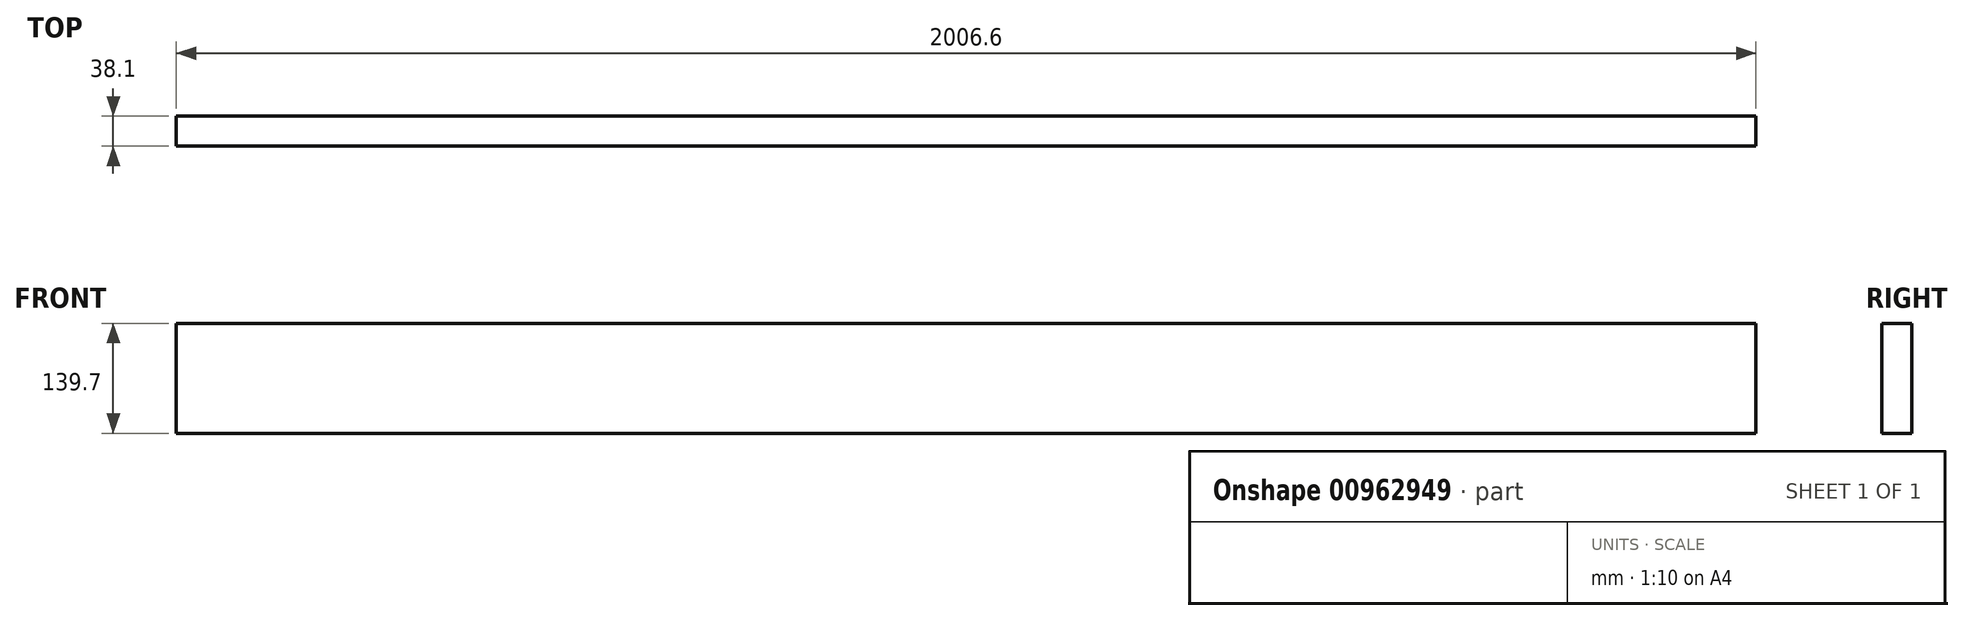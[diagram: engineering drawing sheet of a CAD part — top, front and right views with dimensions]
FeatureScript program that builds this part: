
annotation { "Feature Type Name" : "Feature", "Feature Type Description" : "" }
export const myFeature = defineFeature(function(context is Context, id is Id, definition is map)
    precondition{}
    {
        {
            var Q0;
            Q0=qCreatedBy(makeId("Right.planeOp"),FACE);
            var sketch = newSketch(context, id + "F0", { "sketchPlane" : qUnion([Q0])});
            skLineSegment(sketch, "E0.bottom", {"start": v(-85.59, 94.33) * mm, "end": v(-47.49, 94.33) * mm});
            skLineSegment(sketch, "E0.top", {"start": v(-85.59, -45.37) * mm, "end": v(-47.49, -45.37) * mm});
            skLineSegment(sketch, "E0.left", {"start": v(-85.59, 94.33) * mm, "end": v(-85.59, -45.37) * mm});
            skLineSegment(sketch, "E0.right", {"start": v(-47.49, 94.33) * mm, "end": v(-47.49, -45.37) * mm});
            skSolve(sketch);
        }
        {
            var Q0;
            Q0=makeQuery(id+"F0.imprint","IMPRINT",FACE,{"disambiguationData":[TD([[makeQuery(id+"F0.imprint","IMPRINT",EDGE,{"derivedFrom":sQuery(id+"F0.wireOp",EDGE,"E0.bottom")}),-1.0]])]});
            extrude(context, id + "F1", {"entities" : qUnion([Q0]), "depth" : 2006.6 * mm, "offsetDistance" : 25.4 * mm});
        }
    });
